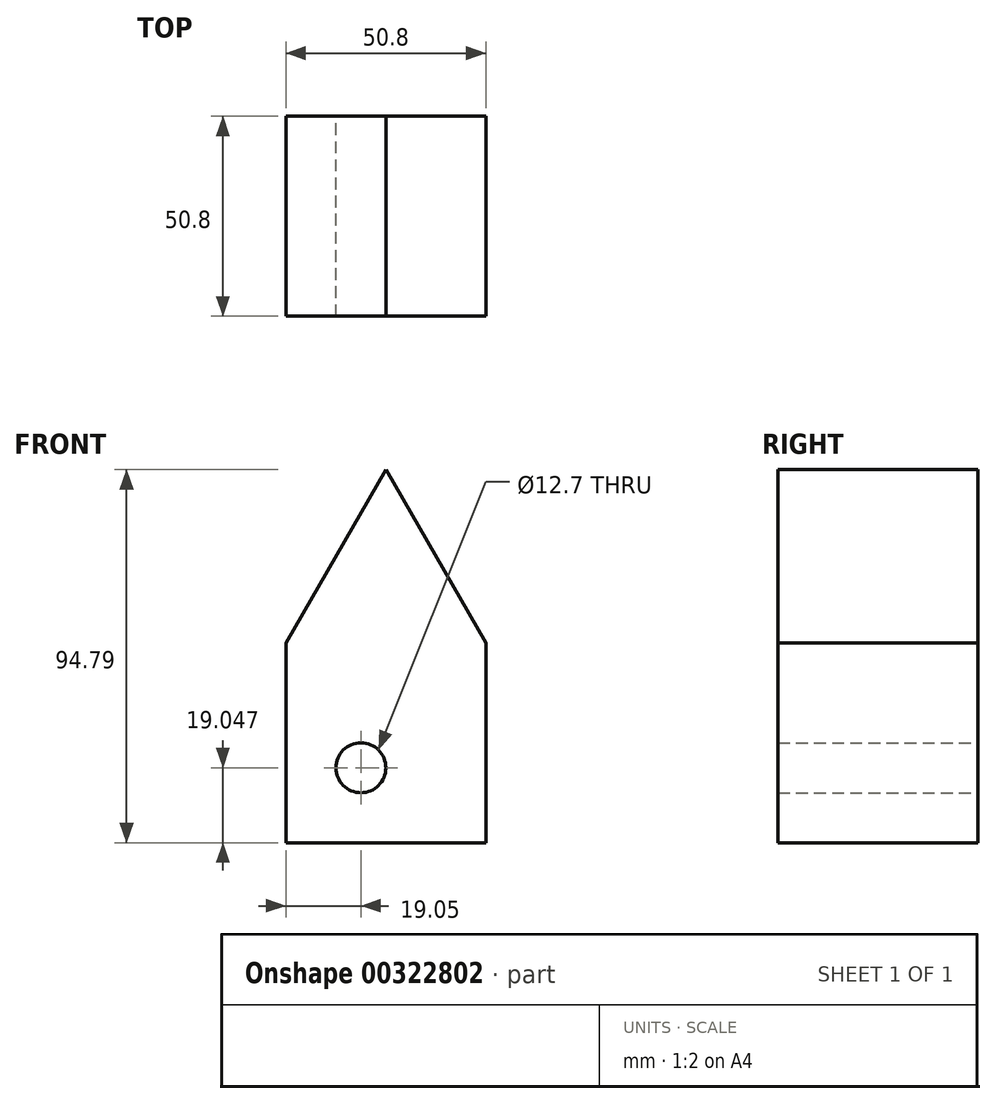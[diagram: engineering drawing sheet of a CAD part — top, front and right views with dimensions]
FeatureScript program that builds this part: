
annotation { "Feature Type Name" : "Feature", "Feature Type Description" : "" }
export const myFeature = defineFeature(function(context is Context, id is Id, definition is map)
    precondition{}
    {
        {
            var Q0;
            Q0=qCreatedBy(makeId("Front.planeOp"),FACE);
            var sketch = newSketch(context, id + "F0", { "sketchPlane" : qUnion([Q0])});
            skLineSegment(sketch, "E0.top", {"start": v(-25.4, -24.23) * mm, "end": v(25.4, -24.23) * mm});
            skLineSegment(sketch, "E0.left", {"start": v(-25.4, 26.57) * mm, "end": v(-25.4, -24.23) * mm});
            skLineSegment(sketch, "E0.right", {"start": v(25.4, 26.57) * mm, "end": v(25.4, -24.23) * mm});
            skLineSegment(sketch, "E1", {"start": v(-25.4, 26.57) * mm, "end": v(0, 70.56) * mm});
            skLineSegment(sketch, "E2", {"start": v(25.4, 26.57) * mm, "end": v(0, 70.56) * mm});
            skCircle(sketch, "E3", {"center": v(-6.35, -5.18) * mm, "radius": 6.35 * mm});
            skSolve(sketch);
        }
        {
            var Q0;
            Q0=makeQuery(id+"F0.imprint","IMPRINT",FACE,{"disambiguationData":[TD([[makeQuery(id+"F0.imprint","IMPRINT",EDGE,{"derivedFrom":sQuery(id+"F0.wireOp",EDGE,"E0.top")}),1.0]])]});
            extrude(context, id + "F1", {"entities" : qUnion([Q0]), "depth" : 50.8 * mm});
        }
    });
